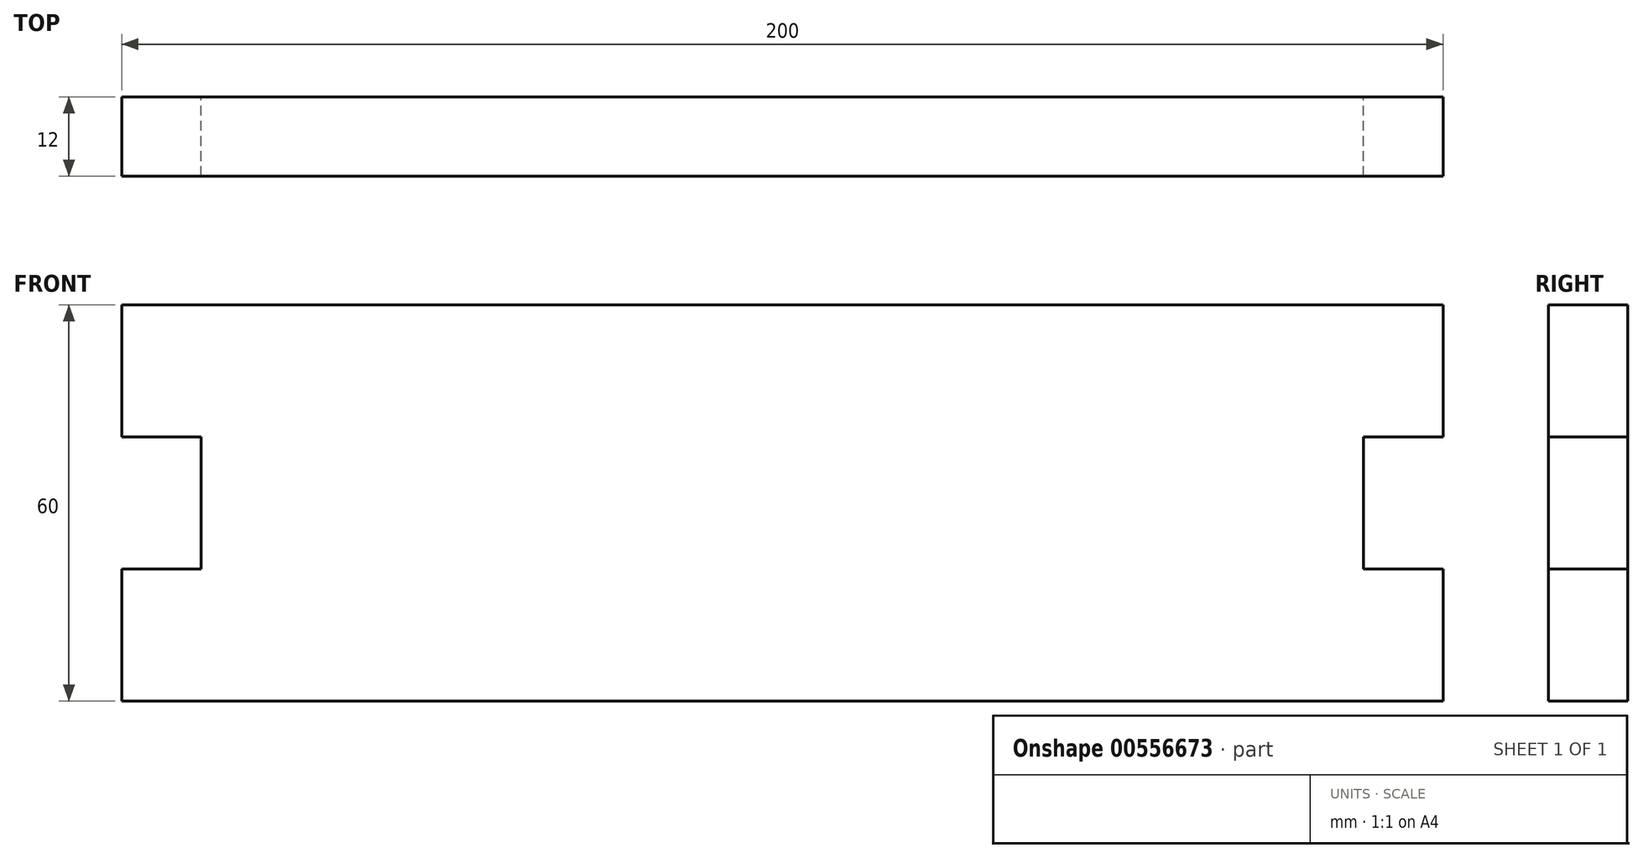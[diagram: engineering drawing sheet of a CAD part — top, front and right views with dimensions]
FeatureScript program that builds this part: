
annotation { "Feature Type Name" : "Feature", "Feature Type Description" : "" }
export const myFeature = defineFeature(function(context is Context, id is Id, definition is map)
    precondition{}
    {
        {
            var Q0;
            Q0=qCreatedBy(makeId("Front.planeOp"),FACE);
            var sketch = newSketch(context, id + "F0", { "sketchPlane" : qUnion([Q0])});
            skLineSegment(sketch, "E0", {"start": v(0, 0) * mm, "end": v(0, 20) * mm});
            skLineSegment(sketch, "E1", {"start": v(0, 20) * mm, "end": v(12, 20) * mm});
            skLineSegment(sketch, "E2", {"start": v(12, 20) * mm, "end": v(12, 40) * mm});
            skLineSegment(sketch, "E3", {"start": v(12, 40) * mm, "end": v(0, 40) * mm});
            skLineSegment(sketch, "E4", {"start": v(0, 40) * mm, "end": v(0, 60) * mm});
            skLineSegment(sketch, "E5", {"start": v(0, 60) * mm, "end": v(100, 60) * mm});
            skLineSegment(sketch, "E6", {"start": v(100, 60) * mm, "end": v(100, 0) * mm, "construction": true});
            skLineSegment(sketch, "E7", {"start": v(100, 0) * mm, "end": v(0, 0) * mm});
            skLineSegment(sketch, "E8.MirrorCS", {"start": v(188, 40) * mm, "end": v(200, 40) * mm});
            skLineSegment(sketch, "E9.MirrorCS", {"start": v(200, 20) * mm, "end": v(188, 20) * mm});
            skLineSegment(sketch, "E10.MirrorCS", {"start": v(100, 0) * mm, "end": v(200, 0) * mm});
            skLineSegment(sketch, "E11.MirrorCS", {"start": v(200, 40) * mm, "end": v(200, 60) * mm});
            skLineSegment(sketch, "E12.MirrorCS", {"start": v(200, 60) * mm, "end": v(100, 60) * mm});
            skLineSegment(sketch, "E13.MirrorCS", {"start": v(188, 20) * mm, "end": v(188, 40) * mm});
            skLineSegment(sketch, "E14.MirrorCS", {"start": v(200, 0) * mm, "end": v(200, 20) * mm});
            skSolve(sketch);
        }
        {
            var Q0;
            Q0 = qSketchRegion(id + "F0", true);
            extrude(context, id + "F1", {"entities" : qUnion([Q0]), "endBound" : BoundingType.SYMMETRIC, "depth" : 12 * mm, "offsetDistance" : 25 * mm});
        }
    });
